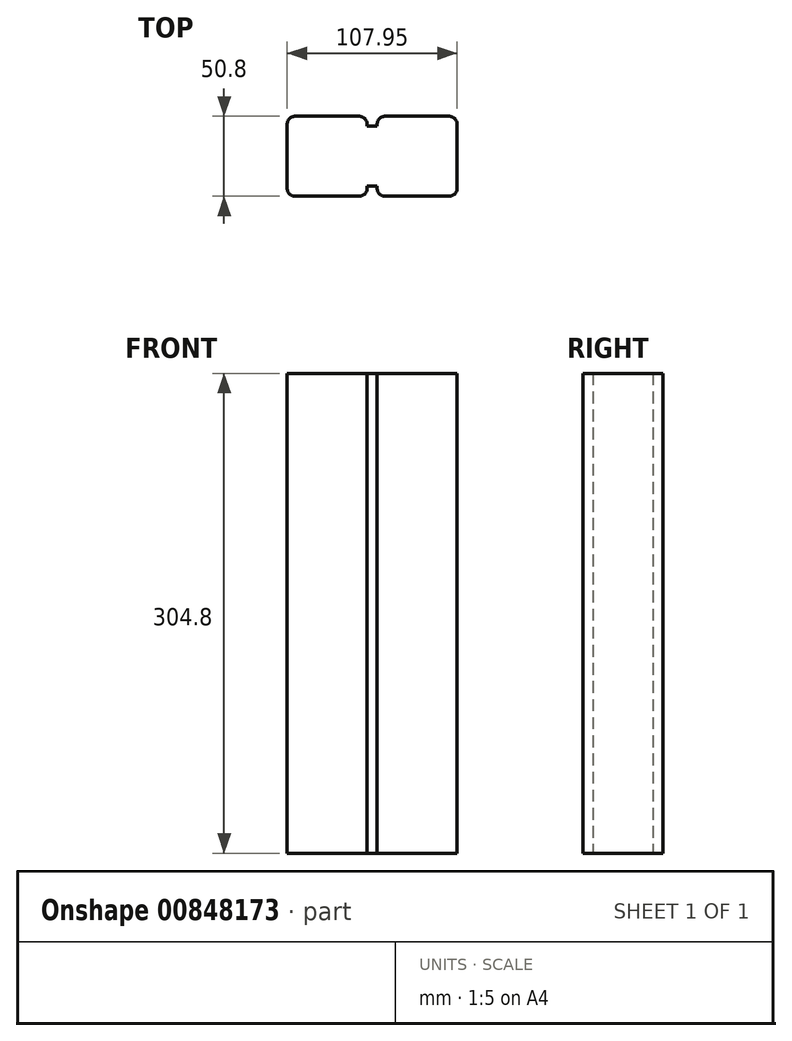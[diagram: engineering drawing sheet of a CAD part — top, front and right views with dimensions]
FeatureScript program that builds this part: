
annotation { "Feature Type Name" : "Feature", "Feature Type Description" : "" }
export const myFeature = defineFeature(function(context is Context, id is Id, definition is map)
    precondition{}
    {
        {
            var Q0;
            Q0=qCreatedBy(makeId("Top.planeOp"),FACE);
            var sketch = newSketch(context, id + "F0", { "sketchPlane" : qUnion([Q0])});
            skLineSegment(sketch, "E0.bottom", {"start": v(0, 0) * mm, "end": v(50.8, 0) * mm});
            skLineSegment(sketch, "E0.top", {"start": v(0, -50.8) * mm, "end": v(50.8, -50.8) * mm});
            skLineSegment(sketch, "E0.left", {"start": v(0, 0) * mm, "end": v(0, -50.8) * mm});
            skLineSegment(sketch, "E0.right", {"start": v(50.8, 0) * mm, "end": v(50.8, -50.8) * mm});
            skSolve(sketch);
        }
        {
            var Q0;
            Q0=makeQuery(id+"F0.imprint","IMPRINT",FACE,{"disambiguationData":[TD([[makeQuery(id+"F0.imprint","IMPRINT",EDGE,{"derivedFrom":sQuery(id+"F0.wireOp",EDGE,"E0.bottom")}),-1.0]])]});
            extrude(context, id + "F1", {"entities" : qUnion([Q0]), "depth" : 304.8 * mm, "offsetDistance" : 25.4 * mm});
        }
        {
            var Q0;
            Q0=makeQuery(id+"F1.opExtrude","SWEPT_EDGE",EDGE,{"disambiguationData":[OSD([sQuery(id+"F0.wireOp",EDGE,"E0.top"),sQuery(id+"F0.wireOp",EDGE,"E0.left")])]});
            var Q1;
            Q1=makeQuery(id+"F1.opExtrude","SWEPT_EDGE",EDGE,{"disambiguationData":[OSD([sQuery(id+"F0.wireOp",EDGE,"E0.top"),sQuery(id+"F0.wireOp",EDGE,"E0.right")])]});
            var Q2;
            Q2=makeQuery(id+"F1.opExtrude","SWEPT_EDGE",EDGE,{"disambiguationData":[OSD([sQuery(id+"F0.wireOp",EDGE,"E0.bottom"),sQuery(id+"F0.wireOp",EDGE,"E0.right")])]});
            var Q3;
            Q3=makeQuery(id+"F1.opExtrude","SWEPT_EDGE",EDGE,{"disambiguationData":[OSD([sQuery(id+"F0.wireOp",EDGE,"E0.bottom"),sQuery(id+"F0.wireOp",EDGE,"E0.left")])]});
            fillet(context, id + "F2", {"entities" : qUnion([Q0, Q1, Q2, Q3]), "radius" : 5.08 * mm, "tangentPropagation" : true, "allowEdgeOverflow" : false});
        }
        {
            var Q0;
            Q0=qCreatedBy(makeId("Top.planeOp"),FACE);
            var sketch = newSketch(context, id + "F3", { "sketchPlane" : qUnion([Q0])});
            skLineSegment(sketch, "E1.bottom", {"start": v(0, -6.35) * mm, "end": v(-6.35, -6.35) * mm});
            skLineSegment(sketch, "E1.top", {"start": v(0, -44.45) * mm, "end": v(-6.35, -44.45) * mm});
            skLineSegment(sketch, "E1.left", {"start": v(0, -6.35) * mm, "end": v(0, -44.45) * mm});
            skLineSegment(sketch, "E1.right", {"start": v(-6.35, -6.35) * mm, "end": v(-6.35, -44.45) * mm});
            skSolve(sketch);
        }
        {
            var Q0;
            Q0=makeQuery(id+"F3.imprint","IMPRINT",FACE,{"disambiguationData":[TD([[makeQuery(id+"F3.imprint","IMPRINT",EDGE,{"derivedFrom":sQuery(id+"F3.wireOp",EDGE,"E1.bottom")}),1.0]])]});
            extrude(context, id + "F4", {"entities" : qUnion([Q0]), "operationType" : NewBodyOperationType.ADD, "depth" : 304.8 * mm, "offsetDistance" : 25.4 * mm});
        }
        {
            var Q0;
            Q0=qCreatedBy(makeId("Top.planeOp"),FACE);
            var sketch = newSketch(context, id + "F5", { "sketchPlane" : qUnion([Q0])});
            skLineSegment(sketch, "E2.bottom", {"start": v(-6.35, 0) * mm, "end": v(-57.15, 0) * mm});
            skLineSegment(sketch, "E2.top", {"start": v(-6.35, -50.8) * mm, "end": v(-57.15, -50.8) * mm});
            skLineSegment(sketch, "E2.left", {"start": v(-6.35, 0) * mm, "end": v(-6.35, -50.8) * mm});
            skLineSegment(sketch, "E2.right", {"start": v(-57.15, 0) * mm, "end": v(-57.15, -50.8) * mm});
            skSolve(sketch);
        }
        {
            var Q0;
            Q0=makeQuery(id+"F5.imprint","IMPRINT",FACE,{"disambiguationData":[TD([[makeQuery(id+"F5.imprint","IMPRINT",EDGE,{"derivedFrom":sQuery(id+"F5.wireOp",EDGE,"E2.bottom")}),1.0]])]});
            extrude(context, id + "F6", {"entities" : qUnion([Q0]), "operationType" : NewBodyOperationType.ADD, "depth" : 304.8 * mm, "offsetDistance" : 25.4 * mm});
        }
        {
            var Q0;
            Q0=makeQuery(id+"F6.opExtrude","SWEPT_EDGE",EDGE,{"disambiguationData":[OSD([sQuery(id+"F5.wireOp",EDGE,"E2.top"),sQuery(id+"F5.wireOp",EDGE,"E2.right")])]});
            var Q1;
            Q1=makeQuery(id+"F6.opExtrude","SWEPT_EDGE",EDGE,{"disambiguationData":[OSD([sQuery(id+"F5.wireOp",EDGE,"E2.top"),sQuery(id+"F5.wireOp",EDGE,"E2.left")])]});
            var Q2;
            Q2=makeQuery(id+"F6.opExtrude","SWEPT_EDGE",EDGE,{"disambiguationData":[OSD([sQuery(id+"F5.wireOp",EDGE,"E2.bottom"),sQuery(id+"F5.wireOp",EDGE,"E2.right")])]});
            var Q3;
            Q3=makeQuery(id+"F6.opExtrude","SWEPT_EDGE",EDGE,{"disambiguationData":[OSD([sQuery(id+"F5.wireOp",EDGE,"E2.bottom"),sQuery(id+"F5.wireOp",EDGE,"E2.left")])]});
            fillet(context, id + "F7", {"entities" : qUnion([Q0, Q1, Q2, Q3]), "radius" : 5.08 * mm, "tangentPropagation" : true, "allowEdgeOverflow" : false});
        }
    });
